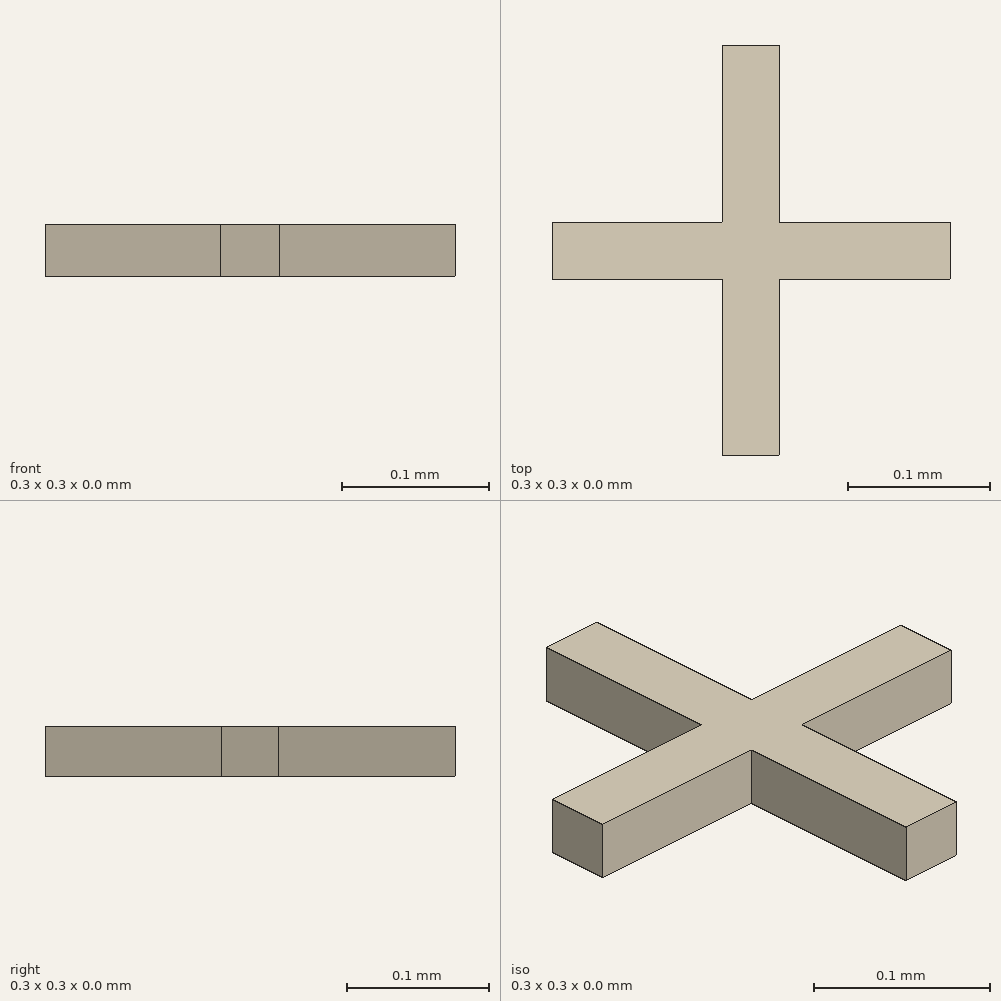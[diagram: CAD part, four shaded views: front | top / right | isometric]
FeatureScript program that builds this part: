
annotation { "Feature Type Name" : "Feature", "Feature Type Description" : "" }
export const myFeature = defineFeature(function(context is Context, id is Id, definition is map)
    precondition{}
    {
        {
            var Q0;
            Q0=qCreatedBy(makeId("Top.planeOp"),FACE);
            var sketch = newSketch(context, id + "F0", { "sketchPlane" : qUnion([Q0])});
            skText(sketch, "E0", { "text": "+", "fontName": "OpenSans-Regular.ttf"});
            const initialGuessF0  = {"E0": [-0.00018, -0.00022, 1, 0, 0.00043]};
            skSetInitialGuess(sketch, initialGuessF0);
            skSolve(sketch);
        }
        {
            var Q0;
            Q0 = qSketchRegion(id + "F0", true);
            extrude(context, id + "F1", {"entities" : qUnion([Q0]), "depth" : 0.04 * mm});
        }
    });
